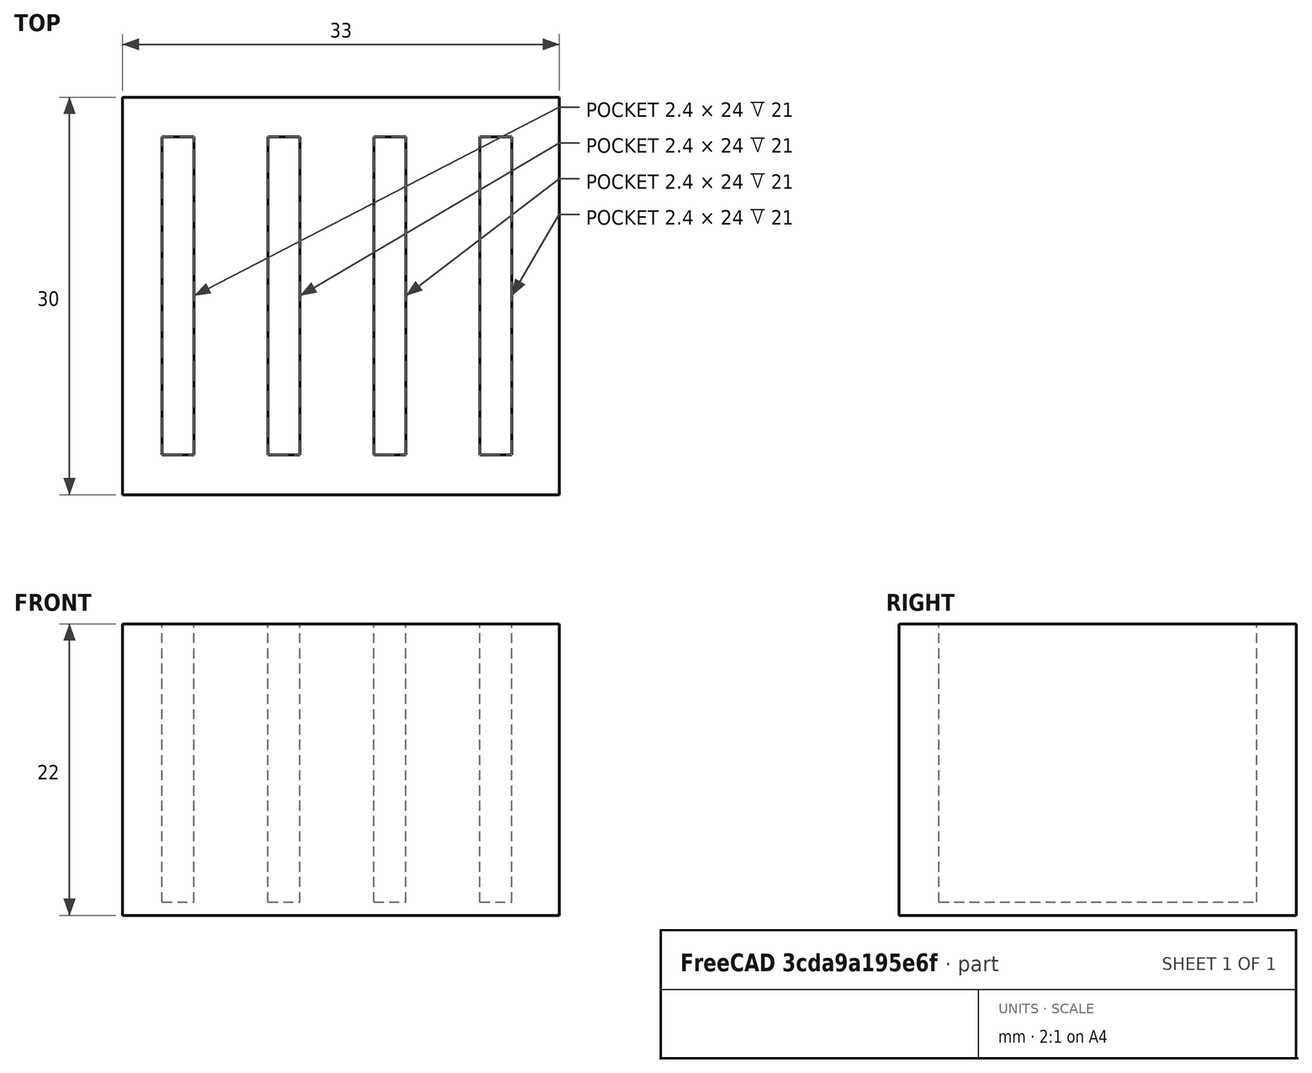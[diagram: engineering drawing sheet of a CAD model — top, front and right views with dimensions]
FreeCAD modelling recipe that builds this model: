
FCSTD DOCUMENT  (FreeCAD 0.21R33694 (Git))
Label: OJT1_T08_R02Portasds
License: All rights reserved
LicenseURL: https://en.wikipedia.org/wiki/All_rights_reserved
objects: Part::Box×5, Part::MultiFuse×1, Part::Cut×1
note: 7 computed .brp shape members not serialized (recipe doc carries the construction recipe); baked Part::Feature solids carry a one-line shape summary decoded from their .brp

FEATURE [Part::Box] Box  label="Ranura1"
  AttacherType = Attacher::AttachEngine3D
  Height = 22
  Length = 2.4
  Width = 24
  expr: .Placement.Base.x = 0 mm
FEATURE [Part::Box] Box001  label="Ranura002"
  AttacherType = Attacher::AttachEngine3D
  Height = 22
  Length = 2.4
  Placement = pos=(8,0,0) rot=(0,0,1;0rad)
  Width = 24
  expr: .Placement.Base.x = 8
FEATURE [Part::Box] Box002  label="Ranura003"
  AttacherType = Attacher::AttachEngine3D
  Height = 22
  Length = 2.4
  Placement = pos=(16,0,0) rot=(0,0,1;0rad)
  Width = 24
  expr: .Placement.Base.x = 16
FEATURE [Part::Box] Box003  label="Ranura004"
  AttacherType = Attacher::AttachEngine3D
  Height = 22
  Length = 2.4
  Placement = pos=(24,0,0) rot=(0,0,1;0rad)
  Width = 24
  expr: .Placement.Base.x = 24
FEATURE [Part::MultiFuse] Fusion
  Placement = pos=(3,3,1) rot=(0,0,1;0rad)
  Shapes = -> [Box003,Box,Box001,Box002]
FEATURE [Part::Box] Box004  label="Cub"
  AttacherType = Attacher::AttachEngine3D
  Height = 22
  Length = 33
  Width = 30
  expr: .Placement.Base.x = 0
  expr: .Placement.Base.y = 0
FEATURE [Part::Cut] Cut
  Base = -> Box004
  Tool = -> Fusion
